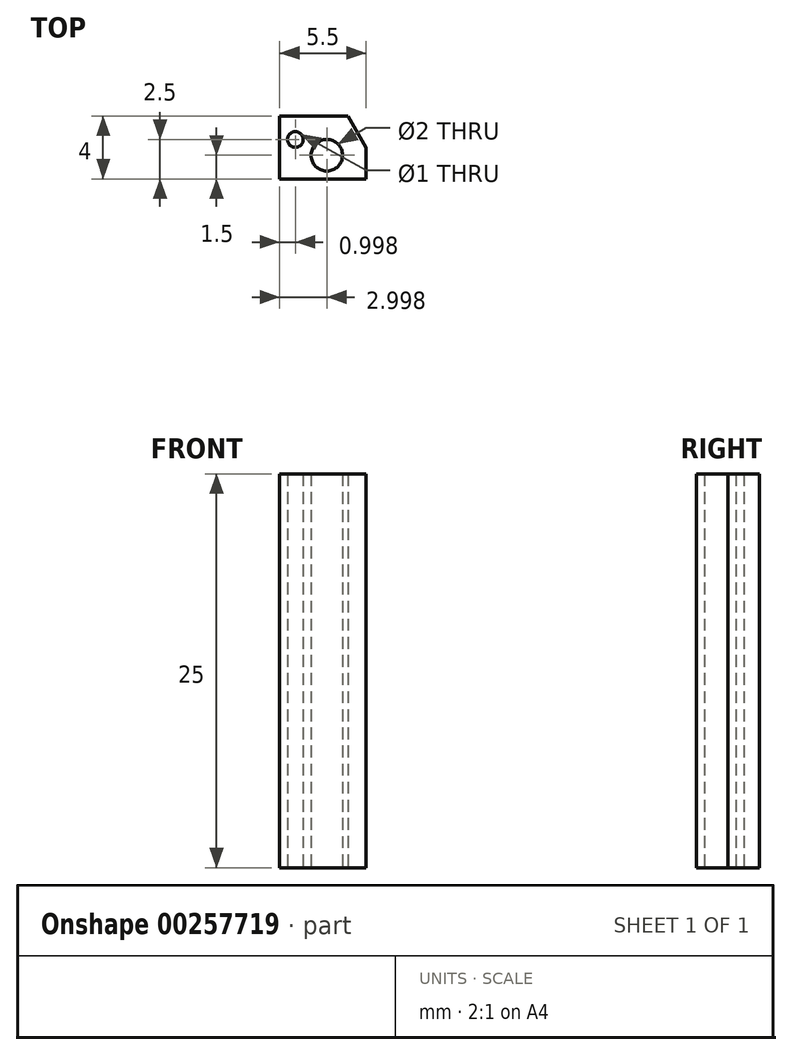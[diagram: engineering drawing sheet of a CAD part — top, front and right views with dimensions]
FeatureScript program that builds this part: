
annotation { "Feature Type Name" : "Feature", "Feature Type Description" : "" }
export const myFeature = defineFeature(function(context is Context, id is Id, definition is map)
    precondition{}
    {
        {
            var Q0;
            Q0=qCreatedBy(makeId("Top.planeOp"),FACE);
            var sketch = newSketch(context, id + "F0", { "sketchPlane" : qUnion([Q0])});
            skLineSegment(sketch, "E0", {"start": v(-3.32, -52.03) * mm, "end": v(2.18, -52.03) * mm});
            skLineSegment(sketch, "E1", {"start": v(-3.32, -52.03) * mm, "end": v(-3.32, -48.03) * mm});
            skLineSegment(sketch, "E2", {"start": v(2.18, -52.03) * mm, "end": v(2.18, -50.03) * mm});
            skLineSegment(sketch, "E3", {"start": v(2.18, -50.03) * mm, "end": v(1.02, -48.03) * mm});
            skLineSegment(sketch, "E4", {"start": v(-3.32, -48.03) * mm, "end": v(1.02, -48.03) * mm});
            skPoint(sketch, "E5.end.orphan", {"position": v(2.18, -48.03) * mm});
            skCircle(sketch, "E6", {"center": v(-0.32, -50.53) * mm, "radius": 0.5 * mm});
            skCircle(sketch, "E7", {"center": v(-0.32, -50.53) * mm, "radius": 1 * mm});
            skCircle(sketch, "E8", {"center": v(-2.32, -49.53) * mm, "radius": 0.5 * mm});
            skSolve(sketch);
        }
        {
            var Q0;
            Q0 = qSketchRegion(id + "F0", true);
            extrude(context, id + "F1", {"entities" : qUnion([Q0]), "depth" : 25 * mm});
        }
    });
